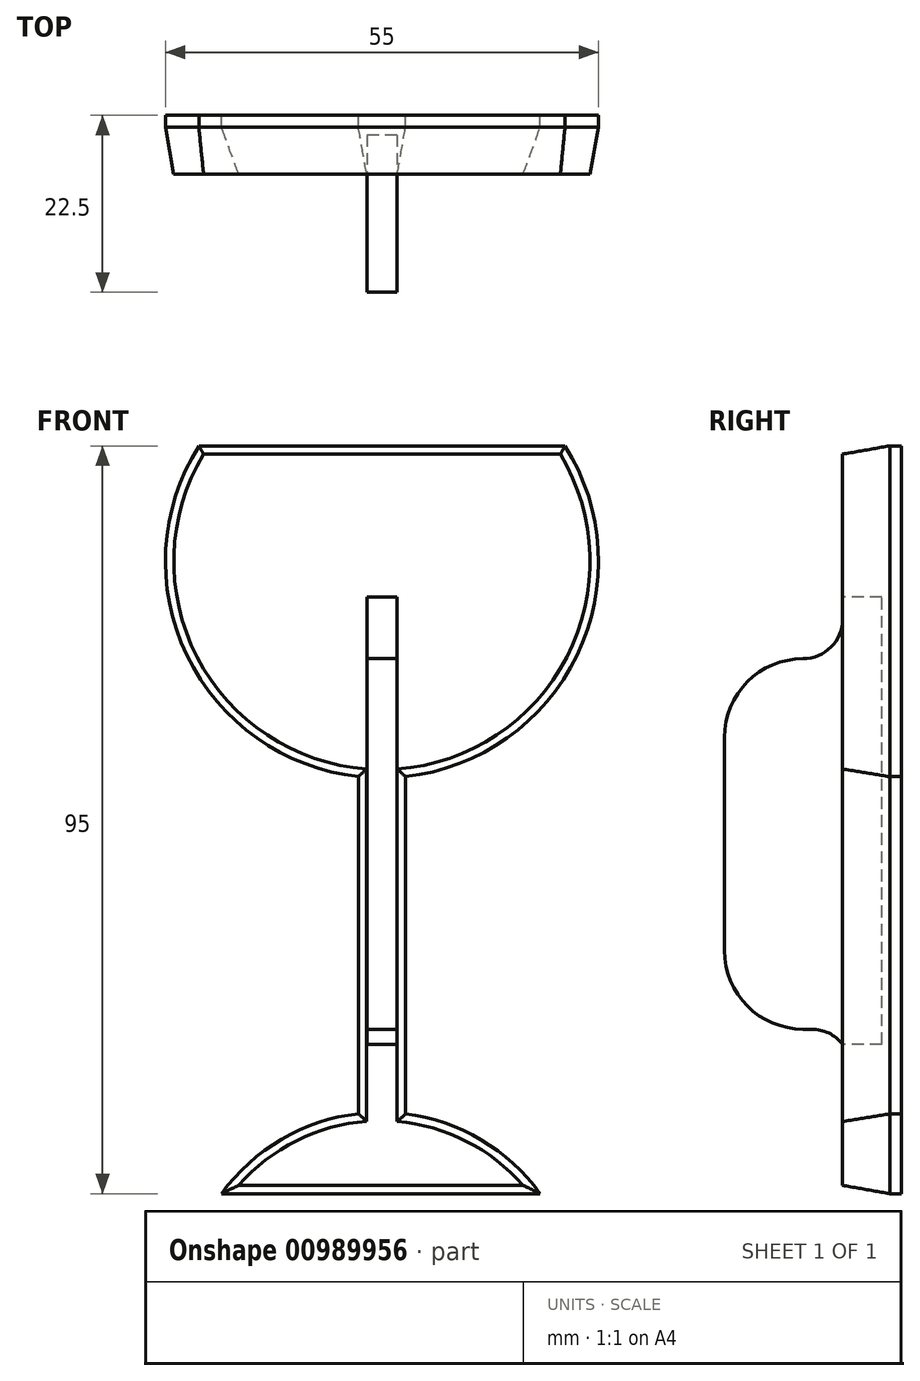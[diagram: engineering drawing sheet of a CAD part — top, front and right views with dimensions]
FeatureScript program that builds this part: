
annotation { "Feature Type Name" : "Feature", "Feature Type Description" : "" }
export const myFeature = defineFeature(function(context is Context, id is Id, definition is map)
    precondition{}
    {
        {
            var Q0;
            Q0=qCreatedBy(makeId("Front.planeOp"),FACE);
            var sketch = newSketch(context, id + "F0", { "sketchPlane" : qUnion([Q0])});
            skArc(sketch, "E0", {"start": v(-23.25, 68.77) * mm, "mid": v(-24.77, 42.15) * mm, "end": v(-3, 26.76) * mm});
            skArc(sketch, "E1", {"start": v(20.1, -26.23) * mm, "mid": v(12.6, -19.4) * mm, "end": v(3, -16.1) * mm});
            skLineSegment(sketch, "E2", {"start": v(-23.25, 68.77) * mm, "end": v(23.25, 68.77) * mm});
            skLineSegment(sketch, "E3", {"start": v(0, 68.77) * mm, "end": v(0, -26.23) * mm, "construction": true});
            skArc(sketch, "E4.trimOffspring", {"start": v(3, 26.76) * mm, "mid": v(24.77, 42.15) * mm, "end": v(23.25, 68.77) * mm});
            skArc(sketch, "E5.trimOffspring", {"start": v(-3, -16.07) * mm, "mid": v(-12.76, -19.33) * mm, "end": v(-20.38, -26.23) * mm});
            skLineSegment(sketch, "E6", {"start": v(-3, 26.76) * mm, "end": v(-3, -16.07) * mm});
            skLineSegment(sketch, "E7", {"start": v(3, -16.1) * mm, "end": v(3, 26.76) * mm});
            skLineSegment(sketch, "E8", {"start": v(20.1, -26.23) * mm, "end": v(-20.38, -26.23) * mm});
            skSolve(sketch);
        }
        {
            var Q0;
            {var subQ0=sQuery(id+"F0.wireOp",EDGE,"E0");Q0=makeQuery(id+"F0.imprint","IMPRINT",FACE,{"disambiguationData":[TD([[makeQuery(id+"F0.imprint","IMPRINT",EDGE,{"derivedFrom":subQ0}),1.0]])]});}
            extrude(context, id + "F1", {"entities" : qUnion([Q0]), "depth" : 1.5 * mm, "offsetDistance" : 25 * mm});
        }
        {
            var Q0;
            Q0=makeQuery(id+"F1.opExtrude","CAP_FACE",FACE,{"disambiguationData":[OSD([sQuery(id+"F0.wireOp",EDGE,"E0"),sQuery(id+"F0.wireOp",EDGE,"E1"),sQuery(id+"F0.wireOp",EDGE,"14a9022b-60d1-404d-8eda-2d7acb7c6140"),sQuery(id+"F0.wireOp",EDGE,"E2"),sQuery(id+"F0.wireOp",EDGE,"ipmtpaCN-cQwt-7Lit-iXcp-3kiPpXHDUtTe"),sQuery(id+"F0.wireOp",EDGE,"4c4fdd56-e103-4abc-aa39-68e74de130950.MirrorCS"),sQuery(id+"F0.wireOp",EDGE,"E4.trimOffspring"),sQuery(id+"F0.wireOp",EDGE,"E5.trimOffspring")])],"isStart":false});
            extrude(context, id + "F2", {"entities" : qUnion([Q0]), "operationType" : NewBodyOperationType.ADD, "depth" : 6 * mm, "offsetDistance" : 25 * mm, "hasDraft" : true, "draftAngle" : 10 * degree, "draftPullDirection" : true});
        }
        {
            var Q0;
            Q0=qCreatedBy(makeId("Right.planeOp"),FACE);
            var sketch = newSketch(context, id + "F3", { "sketchPlane" : qUnion([Q0])});
            skLineSegment(sketch, "E9.bottom", {"start": v(-7.5, -5.33) * mm, "end": v(-22.5, -5.33) * mm});
            skLineSegment(sketch, "E9.top", {"start": v(-7.5, 41.73) * mm, "end": v(-22.5, 41.73) * mm});
            skLineSegment(sketch, "E9.right", {"start": v(-22.5, -5.33) * mm, "end": v(-22.5, 41.73) * mm});
            skLineSegment(sketch, "E10.top", {"start": v(-2.5, -7.24) * mm, "end": v(-7.5, -7.24) * mm});
            skLineSegment(sketch, "E10.right", {"start": v(-7.5, -5.33) * mm, "end": v(-7.5, -7.24) * mm});
            skLineSegment(sketch, "E11.top", {"start": v(-2.5, 49.56) * mm, "end": v(-7.5, 49.56) * mm});
            skLineSegment(sketch, "E11.right", {"start": v(-7.5, 49.56) * mm, "end": v(-7.5, 41.73) * mm});
            skLineSegment(sketch, "E12", {"start": v(-2.5, -7.24) * mm, "end": v(-2.5, 49.56) * mm});
            skSolve(sketch);
        }
        {
            var Q0;
            Q0=makeQuery(id+"F3.imprint","IMPRINT",FACE,{"disambiguationData":[TD([[makeQuery(id+"F3.imprint","IMPRINT",EDGE,{"derivedFrom":sQuery(id+"F3.wireOp",EDGE,"E9.bottom")}),-1.0]])]});
            var Q1;
            Q1=makeQuery(id+"F2.opExtrude","SWEPT_FACE",FACE,{"disambiguationData":[OSD([sQuery(id+"F0.wireOp",EDGE,"ipmtpaCN-cQwt-7Lit-iXcp-3kiPpXHDUtTe")])]});
            extrude(context, id + "F4", {"entities" : qUnion([Q0]), "endBound" : BoundingType.SYMMETRIC, "depth" : 3.8 * mm, "endBoundEntityFace" : qUnion([Q1]), "offsetDistance" : 25 * mm});
        }
        {
            var Q0;
            Q0=makeQuery(id+"F4.opExtrude","SWEPT_EDGE",EDGE,{"disambiguationData":[OSD([sQuery(id+"F3.wireOp",EDGE,"E9.bottom"),sQuery(id+"F3.wireOp",EDGE,"E9.right")])]});
            fillet(context, id + "F5", {"entities" : qUnion([Q0]), "radius" : 10 * mm, "tangentPropagation" : true, "allowEdgeOverflow" : false});
        }
        {
            var Q0;
            Q0=makeQuery(id+"F4.opExtrude","SWEPT_EDGE",EDGE,{"disambiguationData":[OSD([sQuery(id+"F3.wireOp",EDGE,"E9.top"),sQuery(id+"F3.wireOp",EDGE,"E9.right")])]});
            fillet(context, id + "F6", {"entities" : qUnion([Q0]), "radius" : 10 * mm, "tangentPropagation" : true, "allowEdgeOverflow" : false});
        }
        {
            var Q0;
            Q0=makeQuery(id+"F4.opExtrude","SWEPT_EDGE",EDGE,{"disambiguationData":[OSD([sQuery(id+"F3.wireOp",EDGE,"E9.bottom"),sQuery(id+"F3.wireOp",EDGE,"E10.right")])]});
            var Q1;
            Q1=makeQuery(id+"F4.opExtrude","SWEPT_EDGE",EDGE,{"disambiguationData":[OSD([sQuery(id+"F3.wireOp",EDGE,"E9.top"),sQuery(id+"F3.wireOp",EDGE,"E11.right")])]});
            fillet(context, id + "F7", {"entities" : qUnion([Q0, Q1]), "radius" : 5 * mm, "tangentPropagation" : true, "allowEdgeOverflow" : false});
        }
    });
